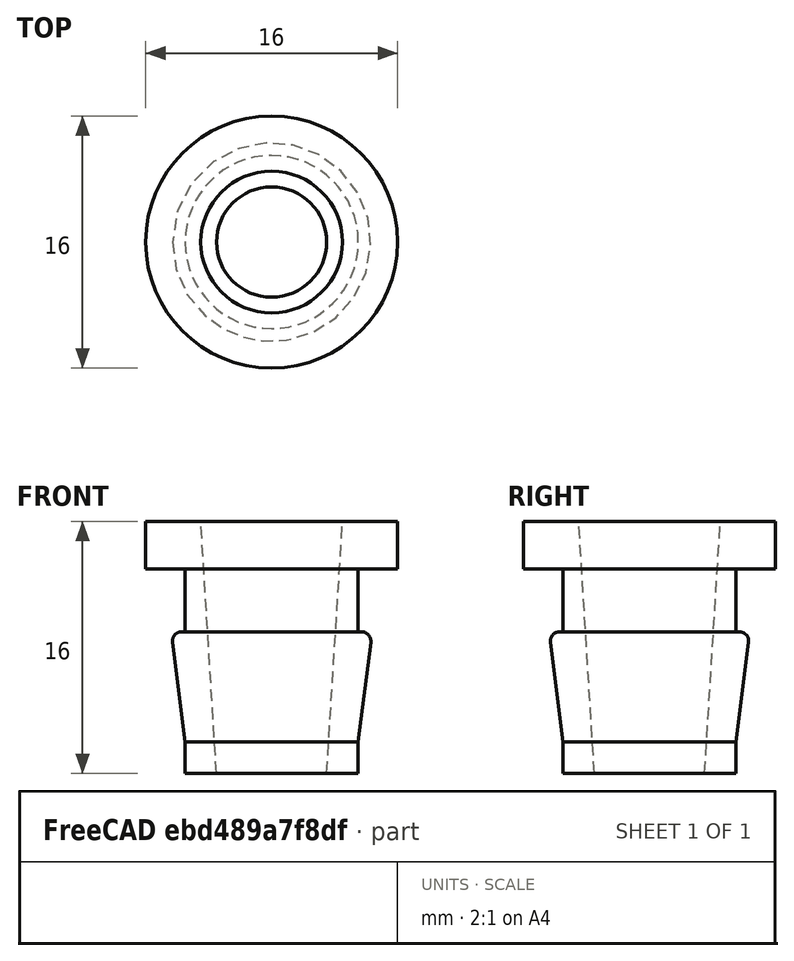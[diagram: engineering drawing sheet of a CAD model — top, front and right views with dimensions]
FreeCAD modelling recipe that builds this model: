
FCSTD DOCUMENT  (FreeCAD 1.0R39285 (Git))
Label: Ext_Box_Gland_2
License: CERN Open Hardware Licence permissive
LicenseURL: https://cern-ohl.web.cern.ch/
objects: Sketcher::SketchObject×1, PartDesign::Revolution×1, PartDesign::Body×1
note: 6 computed .brp shape members not serialized (recipe doc carries the construction recipe); baked Part::Feature solids carry a one-line shape summary decoded from their .brp

FEATURE [Sketcher::SketchObject] Sketch
  ArcFitTolerance = 1e-06
  AttachmentSupport = -> [XZ_Plane]
  FullyConstrained = true
  MakeInternals = false
  MapMode = 5
  Placement = pos=(0,0,0) rot=(1,0,0;1.5708rad)
  sketch-geometry (10):
    g0: LineSegment StartX=-4.5 StartY=16 StartZ=0 EndX=-8 EndY=16 EndZ=0
    g1: LineSegment StartX=-8 StartY=16 StartZ=0 EndX=-8 EndY=13 EndZ=0
    g2: LineSegment StartX=-8 StartY=13 StartZ=0 EndX=-5.5 EndY=13 EndZ=0
    g3: LineSegment StartX=-5.5 StartY=13 StartZ=0 EndX=-5.5 EndY=9 EndZ=0
    g4: LineSegment StartX=-5.5 StartY=9 StartZ=0 EndX=-5.7 EndY=9 EndZ=0
    g5: ArcOfCircle CenterX=-5.7 CenterY=8.4 CenterZ=0 NormalX=0 NormalY=0 NormalZ=1 AngleXU=0 Radius=0.6 StartAngle=1.5708 EndAngle=3.26667
    g6: LineSegment StartX=-6.29531 StartY=8.32515 StartZ=0 EndX=-5.5 EndY=2 EndZ=0
    g7: LineSegment StartX=-5.5 StartY=2 StartZ=0 EndX=-5.5 EndY=0 EndZ=0
    g8: LineSegment StartX=-5.5 StartY=0 StartZ=0 EndX=-3.5 EndY=0 EndZ=0
    g9: LineSegment StartX=-3.5 StartY=0 StartZ=0 EndX=-4.5 EndY=16 EndZ=0
  constraints (29):
    c: Horizontal(g0)
    c: Coincident(g0,g1)
    c: Vertical(g1)
    c: Coincident(g1,g2)
    c: Horizontal(g2)
    c: Coincident(g2,g3)
    c: Vertical(g3)
    c: Coincident(g3,g4)
    c: Horizontal(g4)
    c: Tangent(g4,g5) = -1.5708
    c: Coincident(g6,g7)
    c: Vertical(g7)
    c: Coincident(g7,g8)
    c: Horizontal(g8)
    c: Coincident(g8,g9)
    c: DistanceY(g3,g3) = 4
    c: DistanceY(g1,g1) = 3
    c: DistanceX(g4,g4) = 0.2
    c: DistanceY(g6,g3) = 7
    c: Tangent(g5,g6) = -1.5708
    c: PointOnObject(g8,g-1)
    c: DistanceX(g8,g-1) = 3.5
    c: DistanceX(g9,g-1) = 4.5
    c: Coincident(g0,g9)
    c: Distance(g2,g-2) = 5.5
    c: Distance(g0,g-2) = 8
    c: DistanceY(g-1,g0) = 16
    c: Radius(g5) = 0.6
    c: Vertical(g3,g6)
FEATURE [PartDesign::Revolution] Revolution
  Angle = 360
  Angle2 = 60
  Axis = (0,2e-16,1)
  Base = (0,0,0)
  Placement = pos=(0,0,0) rot=(1,0,0;1.5708rad)
  Profile = -> Sketch
  ReferenceAxis = -> Sketch [V_Axis]
  Refine = true
  Suppressed = false
  Type = 0
FEATURE [PartDesign::Body] Body
  AllowCompound = false
  Group = -> [Sketch,Revolution]
  Origin = -> Origin
  Tip = -> Revolution
